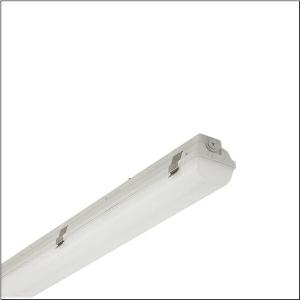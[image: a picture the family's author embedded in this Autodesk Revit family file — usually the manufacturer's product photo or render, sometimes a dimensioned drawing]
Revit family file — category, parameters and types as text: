
# Revit family: monsun_r__21_eco_51fj10mp47a_2b6f
name_source: partatom
category: Lighting Fixtures
units: mm (PartAtom-declared; Revit-internal decimal feet)

## family parameters
Cut with Voids When Loaded = No
Host = Face
Light Source = No
Part Type = Normal
Room Calculation Point = No
Round Connector Dimension = Use Diameter
Shared = No

## types (1)
- --- (1 x LED, 7000 lm, 50 W, 4000K)
    Apparent Load = 50 VA
    CIE Flux Codes = 41 70 89 90 100
    Color Rendering = 80
    Color Temperature = 4000K
    Default Elevation = 1800 mm
    Description = Monsun® 21 Eco, damp-proof luminaire, primary optical cover: diffuser, of PMMA, frosted, light emission: direct distribution, primary light characteristic: symmetric, installation type: suspended mounting, surface-mounted, LED, rated luminous flux: 7.000lm, luminous efficacy: 140lm/W, light colour: 840, colour temperature: 4000K, control gear: ECG Multilumen, with terminal, 3-pole, max. 2.5mm², mains connection: 220..240V, AC, 50/60Hz, rated input power: 50W, housing, of glass-fibre reinforced polyester, light grey (RAL 7035), length: 1.577mm, width: 90mm, height: 95mm, clip for enclosure, of spring steel V2A, protection rating (complete): IP66, insulation class (complete): insulation class I (protective earthing), certification: CE, UKCA, protection symbol: D, impact resistance: IK02, permissible operating ambient temperature: -20..+35°C, corresponds to IFS (International Featured Standards) requirements for safety and quality in the food industry, contact your sales advisor before using the luminaires in applications with unclear chemical exposure, large temperature fluctuations or condensation-forming humidity, packaging unit: 1 piece
    Height = 103 mm
    Lamp = 1 x LED
    Lamp Light Flux = 7000 lm
    Lamp Power = 50 W
    Lamp count = 1
    Length = 1577 mm
    Luminous efficacy = 140 lm/W
    Manufacturer = Siteco
    ModVariant = No
    Model = 51FJ10MP47A
    Mounting Place = Ceiling
    Mounting Type = Surface mounted
    Number of Poles = 1
    OnlyDefault = Yes
    Power Factor = 1
    Product Name = Monsun® 21 Eco
    Product group = damp-proof luminaire
    ProductGroupID = 300
    Protection Class = Protection class I
    Protection Degree = IP 66
    RLX_Detail_Level = 1
    RLX_Emergency_Light_Flux = 0 lm
    RLX_Emergency_Type = 0
    RLX_Emergency_Type_DB = No
    RlxData = <blob elided: 34149 chars, md5=21416670>
    Socket = socket
    Standby Power = 0 W
    System Light Flux = 7000 lm
    System Power = 50 W
    Type Comments = factory setting: luminous flux: 100 % | (ON | ON | ON | ON) | 350 mA
    Type Image = l_1007218.jpg
    URL = http://relux.com
    VarID = @adj_077821
    Voltage = 0 V
    Weight = 0.00 kg
    Width = 90 mm

## geometry (parser evidence)
native form markers: Blend x4, Sweep x13
no freeform markers — native parametric forms only
